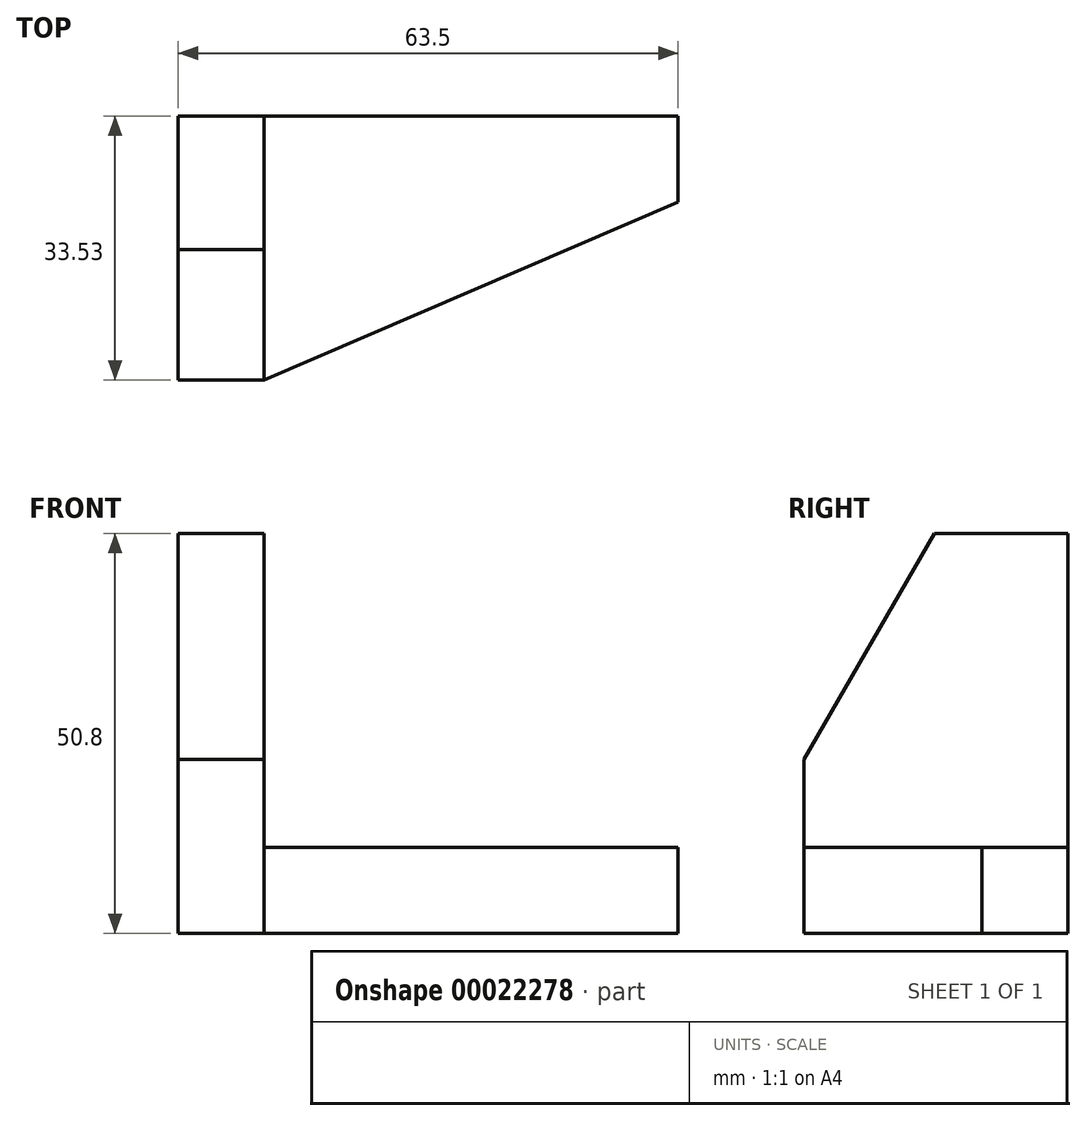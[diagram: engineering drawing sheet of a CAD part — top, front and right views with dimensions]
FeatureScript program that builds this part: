
annotation { "Feature Type Name" : "Feature", "Feature Type Description" : "" }
export const myFeature = defineFeature(function(context is Context, id is Id, definition is map)
    precondition{}
    {
        {
            var Q0;
            Q0=qCreatedBy(makeId("Front.planeOp"),FACE);
            var sketch = newSketch(context, id + "F0", { "sketchPlane" : qUnion([Q0])});
            skLineSegment(sketch, "E0.rect.bottom", {"start": v(-57.15, 30.1) * mm, "end": v(57.15, 30.1) * mm});
            skLineSegment(sketch, "E0.rect.top", {"start": v(-57.15, -30.1) * mm, "end": v(57.15, -30.1) * mm});
            skLineSegment(sketch, "E0.rect.left", {"start": v(-57.15, 30.1) * mm, "end": v(-57.15, -30.1) * mm});
            skLineSegment(sketch, "E0.rect.right", {"start": v(57.15, 30.1) * mm, "end": v(57.15, -30.1) * mm});
            skPoint(sketch, "E0.rect.middle", {"position": v(0, 0) * mm});
            skLineSegment(sketch, "E1.bottom", {"start": v(-57.15, 20.7) * mm, "end": v(-46.23, 20.7) * mm});
            skLineSegment(sketch, "E1.top", {"start": v(-57.15, -30.1) * mm, "end": v(-46.23, -30.1) * mm});
            skLineSegment(sketch, "E1.left", {"start": v(-57.15, 20.7) * mm, "end": v(-57.15, -30.1) * mm});
            skLineSegment(sketch, "E1.right", {"start": v(-46.23, 20.7) * mm, "end": v(-46.23, -30.1) * mm});
            skLineSegment(sketch, "E2.bottom", {"start": v(-46.23, -19.18) * mm, "end": v(6.35, -19.18) * mm});
            skLineSegment(sketch, "E2.top", {"start": v(-46.23, -30.1) * mm, "end": v(6.35, -30.1) * mm});
            skLineSegment(sketch, "E2.left", {"start": v(-46.23, -19.18) * mm, "end": v(-46.23, -30.1) * mm});
            skLineSegment(sketch, "E2.right", {"start": v(6.35, -19.18) * mm, "end": v(6.35, -30.1) * mm});
            skCircle(sketch, "E3", {"center": v(38.1, -11.05) * mm, "radius": 7.87 * mm});
            skLineSegment(sketch, "E4", {"start": v(-25.4, 30.1) * mm, "end": v(57.15, 7.98) * mm});
            skSolve(sketch);
        }
        {
            var Q0;
            Q0=qCreatedBy(makeId("Front.planeOp"),FACE);
            var sketch = newSketch(context, id + "F1", { "sketchPlane" : qUnion([Q0])});
            skLineSegment(sketch, "E5.rect.bottom", {"start": v(-57.15, 30.1) * mm, "end": v(57.15, 30.1) * mm});
            skLineSegment(sketch, "E5.rect.top", {"start": v(-57.15, -30.1) * mm, "end": v(57.15, -30.1) * mm});
            skLineSegment(sketch, "E5.rect.left", {"start": v(-57.15, 30.1) * mm, "end": v(-57.15, -30.1) * mm});
            skLineSegment(sketch, "E5.rect.right", {"start": v(57.15, 30.1) * mm, "end": v(57.15, -30.1) * mm});
            skPoint(sketch, "E5.rect.middle", {"position": v(0, 0) * mm});
            skLineSegment(sketch, "E6", {"start": v(-25.4, 30.1) * mm, "end": v(57.15, 7.98) * mm});
            skLineSegment(sketch, "E7.bottom", {"start": v(-57.15, 20.7) * mm, "end": v(-46.23, 20.7) * mm});
            skLineSegment(sketch, "E7.top", {"start": v(-57.15, -30.1) * mm, "end": v(-46.23, -30.1) * mm});
            skLineSegment(sketch, "E7.left", {"start": v(-57.15, 20.7) * mm, "end": v(-57.15, -30.1) * mm});
            skLineSegment(sketch, "E7.right", {"start": v(-46.23, 20.7) * mm, "end": v(-46.23, -30.1) * mm});
            skSolve(sketch);
        }
        {
            var Q0;
            Q0=makeQuery(id+"F0.imprint","IMPRINT",FACE,{"disambiguationData":[TD([[makeQuery(id+"F0.imprint","IMPRINT",EDGE,{"derivedFrom":sQuery(id+"F0.wireOp",EDGE,"E1.bottom")}),-1.0]])]});
            var Q1;
            {var subQ2=sQuery(id+"F0.wireOp",EDGE,"E0.rect.top");Q1=makeQuery(id+"F0.imprint","IMPRINT",FACE,{"disambiguationData":[TD([[makeQuery(id+"F0.imprint","IMPRINT",EDGE,{"derivedFrom":subQ2}),1.0]])]});}
            var Q2;
            Q2=makeQuery(id+"F0.imprint","IMPRINT",FACE,{"disambiguationData":[TD([[makeQuery(id+"F0.imprint","IMPRINT",EDGE,{"derivedFrom":sQuery(id+"F0.wireOp",EDGE,"E2.bottom")}),-1.0]])]});
            extrude(context, id + "F2", {"entities" : qUnion([Q0, Q1, Q2]), "depth" : 10.92 * mm});
        }
        {
            var Q0;
            Q0=makeQuery(id+"F1.imprint","IMPRINT",FACE,{"disambiguationData":[TD([[makeQuery(id+"F1.imprint","IMPRINT",EDGE,{"derivedFrom":sQuery(id+"F1.wireOp",EDGE,"E7.bottom")}),-1.0]])]});
            extrude(context, id + "F3", {"entities" : qUnion([Q0]), "operationType" : NewBodyOperationType.ADD, "depth" : 33.53 * mm});
        }
        {
            var Q0;
            Q0=makeQuery(id+"F0.imprint","IMPRINT",FACE,{"disambiguationData":[TD([[makeQuery(id+"F0.imprint","IMPRINT",EDGE,{"derivedFrom":sQuery(id+"F0.wireOp",EDGE,"E2.bottom")}),-1.0]])]});
            extrude(context, id + "F4", {"entities" : qUnion([Q0]), "operationType" : NewBodyOperationType.ADD, "depth" : 33.53 * mm});
        }
        {
            var Q0;
            Q0=makeQuery(id+"F3.opExtrude","SWEPT_FACE",FACE,{"disambiguationData":[OSD([sQuery(id+"F1.wireOp",EDGE,"E7.right")])]});
            var sketch = newSketch(context, id + "F5", { "sketchPlane" : qUnion([Q0])});
            skLineSegment(sketch, "E8", {"start": v(-33.53, -8) * mm, "end": v(-16.96, 20.7) * mm});
            skSolve(sketch);
        }
        {
            var Q0;
            Q0 = qSketchRegion(id + "F5", true);
            var Q1;
            {var subQ2=sQuery(id+"F5.wireOp",EDGE,"E8");Q1=makeQuery(id+"F5.imprint","IMPRINT",FACE,{"disambiguationData":[TD([[makeQuery(id+"F5.imprint","IMPRINT",EDGE,{"derivedFrom":subQ2}),1.0]])]});}
            extrude(context, id + "F6", {"entities" : qUnion([Q0, Q1]), "operationType" : NewBodyOperationType.REMOVE, "oppositeDirection" : true, "depth" : 25.4 * mm});
        }
        {
            var Q0;
            Q0=makeQuery(id+"F4.opExtrude","SWEPT_FACE",FACE,{"disambiguationData":[OSD([sQuery(id+"F0.wireOp",EDGE,"E2.bottom")])]});
            var sketch = newSketch(context, id + "F7", { "sketchPlane" : qUnion([Q0])});
            skLineSegment(sketch, "E9", {"start": v(-46.23, -33.53) * mm, "end": v(6.35, -10.92) * mm});
            skSolve(sketch);
        }
        {
            var Q0;
            Q0 = qSketchRegion(id + "F7", true);
            var Q1;
            Q1=makeQuery(id+"F7.imprint","IMPRINT",FACE,{"disambiguationData":[TD([[makeQuery(id+"F7.imprint","IMPRINT",EDGE,{"derivedFrom":sQuery(id+"F7.wireOp",EDGE,"E9")}),-1.0]])]});
            extrude(context, id + "F8", {"entities" : qUnion([Q0, Q1]), "operationType" : NewBodyOperationType.REMOVE, "oppositeDirection" : true, "depth" : 25.4 * mm});
        }
    });
